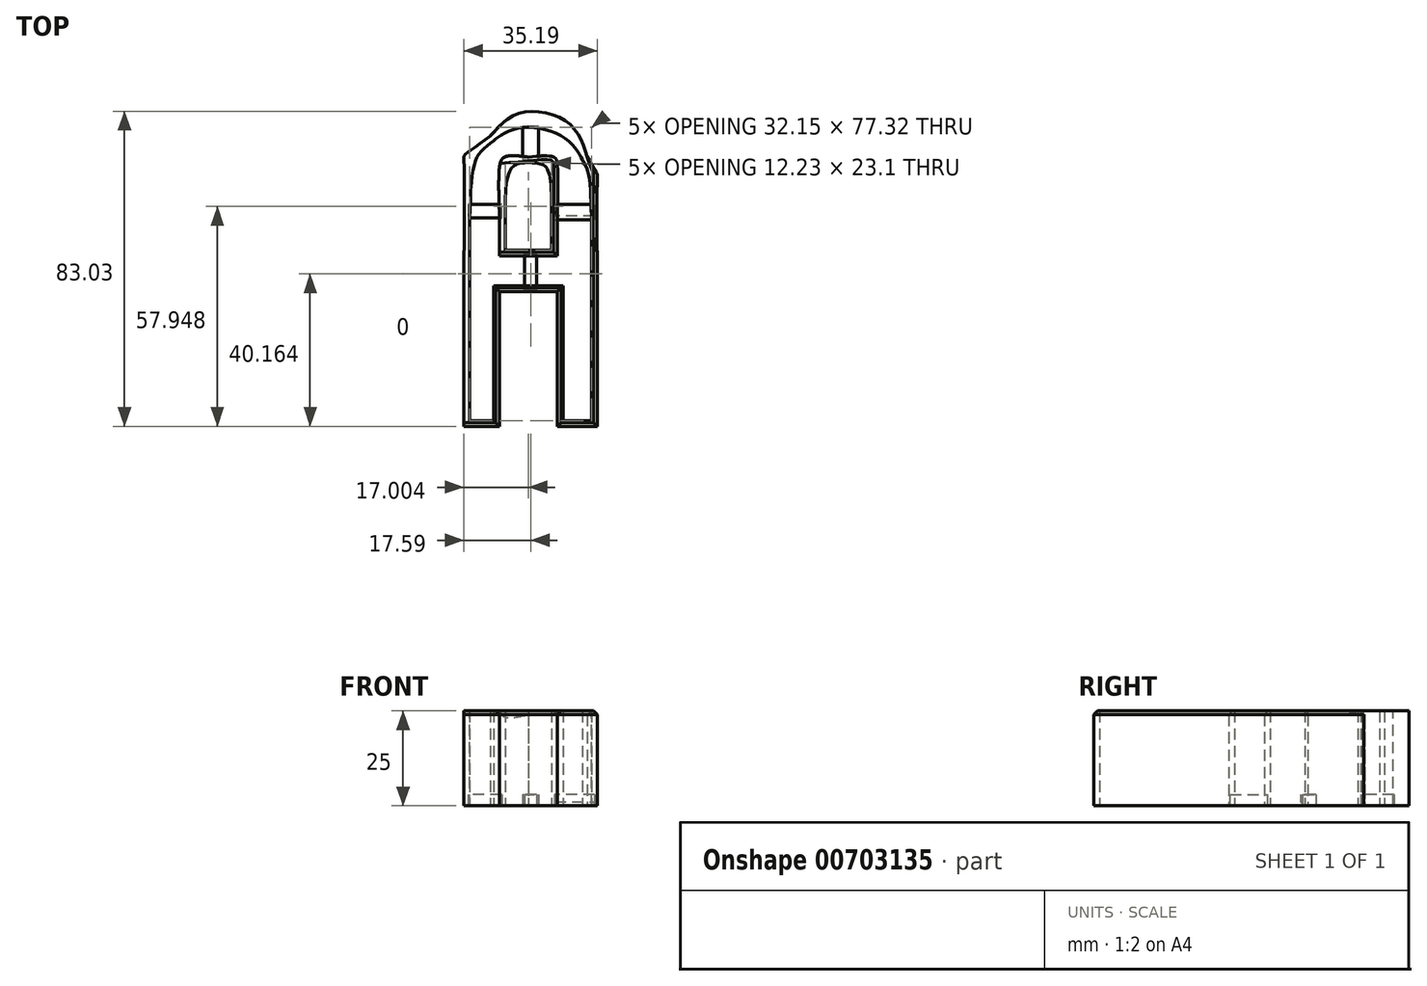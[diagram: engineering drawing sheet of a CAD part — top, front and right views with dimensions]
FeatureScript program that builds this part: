
annotation { "Feature Type Name" : "Feature", "Feature Type Description" : "" }
export const myFeature = defineFeature(function(context is Context, id is Id, definition is map)
    precondition{}
    {
        {
            var Q0;
            Q0=qCreatedBy(makeId("Top.planeOp"),FACE);
            var sketch = newSketch(context, id + "F0", { "sketchPlane" : qUnion([Q0])});
            skLineSegment(sketch, "E0", {"start": v(-8.2, -22.18) * mm, "end": v(-8.2, -4.43) * mm});
            skLineSegment(sketch, "E1", {"start": v(-8.2, -4.43) * mm, "end": v(-0.59, -4.43) * mm});
            skLineSegment(sketch, "E2", {"start": v(-0.59, -4.43) * mm, "end": v(7.03, -4.43) * mm});
            skLineSegment(sketch, "E3", {"start": v(7.03, -4.43) * mm, "end": v(7.03, -22.18) * mm});
            skLineSegment(sketch, "E4", {"start": v(7.03, -22.18) * mm, "end": v(7.03, -39.93) * mm});
            skLineSegment(sketch, "E5", {"start": v(7.03, -39.93) * mm, "end": v(12.3, -39.93) * mm});
            skLineSegment(sketch, "E6", {"start": v(12.3, -39.93) * mm, "end": v(17.58, -39.93) * mm});
            skLineSegment(sketch, "E7", {"start": v(17.58, -39.93) * mm, "end": v(17.58, -6.74) * mm});
            skFitSpline(sketch, "E8", {"points": [v(17.58, -6.74) * mm, v(17.58, 25.6) * mm, v(17.5, 26.57) * mm, v(14.94, 31.1) * mm]});
            skFitSpline(sketch, "E9", {"points": [v(14.94, 31.1) * mm, v(9.84, 40.13) * mm, v(-2.43, 42.74) * mm, v(-10.67, 36.56) * mm]});
            skFitSpline(sketch, "E10", {"points": [v(-10.67, 36.56) * mm, v(-17.53, 31.41) * mm, v(-17.58, 31.15) * mm, v(-17.58, -5.94) * mm]});
            skLineSegment(sketch, "E11", {"start": v(-17.58, -5.94) * mm, "end": v(-17.58, -39.93) * mm});
            skLineSegment(sketch, "E12", {"start": v(-17.58, -39.93) * mm, "end": v(-12.89, -39.93) * mm});
            skLineSegment(sketch, "E13", {"start": v(-12.89, -39.93) * mm, "end": v(-8.2, -39.93) * mm});
            skLineSegment(sketch, "E14", {"start": v(-8.2, -39.93) * mm, "end": v(-8.2, -22.18) * mm});
            skFitSpline(sketch, "E15", {"points": [v(-8.2, 15.7) * mm, v(-8.2, 28.37) * mm, v(-6.87, 31.07) * mm, v(-0.6, 31.07) * mm]});
            skFitSpline(sketch, "E16", {"points": [v(-0.6, 31.07) * mm, v(6.1, 31.07) * mm, v(7.03, 29.27) * mm, v(7.03, 16.38) * mm]});
            skLineSegment(sketch, "E17", {"start": v(7.03, 16.38) * mm, "end": v(7.03, 4.97) * mm});
            skLineSegment(sketch, "E18", {"start": v(7.03, 4.97) * mm, "end": v(-0.59, 4.97) * mm});
            skLineSegment(sketch, "E19", {"start": v(-0.59, 4.97) * mm, "end": v(-8.2, 4.97) * mm});
            skLineSegment(sketch, "E20", {"start": v(-8.2, 4.97) * mm, "end": v(-8.2, 15.7) * mm});
            skLineSegment(sketch, "E21.0", {"start": v(16.08, -38.43) * mm, "end": v(16.08, -6.74) * mm});
            skLineSegment(sketch, "E21.1", {"start": v(12.3, -38.43) * mm, "end": v(16.08, -38.43) * mm});
            skLineSegment(sketch, "E21.2", {"start": v(8.53, -38.43) * mm, "end": v(12.3, -38.43) * mm});
            skLineSegment(sketch, "E21.3", {"start": v(8.53, -22.18) * mm, "end": v(8.53, -38.43) * mm});
            skLineSegment(sketch, "E21.4", {"start": v(-16.08, -38.43) * mm, "end": v(-12.89, -38.43) * mm});
            skLineSegment(sketch, "E21.5", {"start": v(-16.08, -5.94) * mm, "end": v(-16.08, -38.43) * mm});
            skFitSpline(sketch, "E21.6", {"points": [v(-9.77, 35.36) * mm, v(-10.63, 34.71) * mm, v(-11.71, 33.9) * mm, v(-12.8, 32.87) * mm, v(-13.45, 32.1) * mm, v(-14, 31.22) * mm, v(-14.47, 30.16) * mm, v(-14.88, 28.81) * mm, v(-15.34, 26.55) * mm, v(-15.74, 22.7) * mm, v(-15.99, 16) * mm, v(-16.07, 6.81) * mm, v(-16.08, -1.3) * mm, v(-16.08, -5.94) * mm]});
            skFitSpline(sketch, "E21.7", {"points": [v(13.63, 30.37) * mm, v(12.47, 32.43) * mm, v(9.33, 35.8) * mm, v(3.09, 38.5) * mm, v(-3.7, 38.57) * mm, v(-7.9, 36.76) * mm, v(-9.77, 35.36) * mm]});
            skLineSegment(sketch, "E21.8", {"start": v(-12.89, -38.43) * mm, "end": v(-9.7, -38.43) * mm});
            skLineSegment(sketch, "E21.9", {"start": v(-9.7, -38.43) * mm, "end": v(-9.7, -22.18) * mm});
            skLineSegment(sketch, "E21.10", {"start": v(-9.7, -22.18) * mm, "end": v(-9.7, -2.93) * mm});
            skLineSegment(sketch, "E21.11", {"start": v(-9.7, -2.93) * mm, "end": v(-0.59, -2.93) * mm});
            skFitSpline(sketch, "E21.12", {"points": [v(16.08, -6.74) * mm, v(16.08, -2.7) * mm, v(16.07, 4.4) * mm, v(16.04, 12.52) * mm, v(15.93, 18.5) * mm, v(15.74, 22.73) * mm, v(15.44, 25.6) * mm, v(15.02, 27.48) * mm, v(14.47, 28.85) * mm, v(13.95, 29.81) * mm, v(13.63, 30.37) * mm]});
            skLineSegment(sketch, "E21.13", {"start": v(-0.59, -2.93) * mm, "end": v(8.53, -2.93) * mm});
            skLineSegment(sketch, "E21.14", {"start": v(8.53, -2.93) * mm, "end": v(8.53, -22.18) * mm});
            skLineSegment(sketch, "E22.0", {"start": v(-6.7, 6.47) * mm, "end": v(-6.7, 15.7) * mm});
            skFitSpline(sketch, "E22.1", {"points": [v(-0.6, 29.57) * mm, v(0.2, 29.57) * mm, v(1.25, 29.53) * mm, v(2.3, 29.36) * mm, v(2.93, 29.18) * mm, v(3.41, 28.96) * mm, v(3.78, 28.7) * mm, v(4.1, 28.37) * mm, v(4.4, 27.9) * mm, v(4.68, 27.25) * mm, v(5.01, 26.1) * mm, v(5.32, 24.12) * mm, v(5.5, 20.83) * mm, v(5.53, 17.98) * mm, v(5.53, 16.38) * mm]});
            skLineSegment(sketch, "E22.2", {"start": v(5.53, 16.38) * mm, "end": v(5.53, 6.47) * mm});
            skFitSpline(sketch, "E22.3", {"points": [v(-6.7, 15.7) * mm, v(-6.7, 17.27) * mm, v(-6.66, 20.09) * mm, v(-6.44, 23.42) * mm, v(-6.02, 25.91) * mm, v(-5.53, 27.3) * mm, v(-5.07, 28.07) * mm, v(-4.71, 28.5) * mm, v(-4.31, 28.82) * mm, v(-3.84, 29.09) * mm, v(-3.25, 29.3) * mm, v(-2.28, 29.5) * mm, v(-1.33, 29.57) * mm, v(-0.6, 29.57) * mm]});
            skLineSegment(sketch, "E22.4", {"start": v(5.53, 6.47) * mm, "end": v(-0.59, 6.47) * mm});
            skLineSegment(sketch, "E22.5", {"start": v(-0.59, 6.47) * mm, "end": v(-6.7, 6.47) * mm});
            skSolve(sketch);
        }
        {
            var Q0;
            Q0=makeQuery(id+"F0.imprint","IMPRINT",FACE,{"disambiguationData":[TD([[makeQuery(id+"F0.imprint","IMPRINT",EDGE,{"derivedFrom":sQuery(id+"F0.wireOp",EDGE,"E0")}),1.0]])]});
            var Q1;
            Q1=makeQuery(id+"F0.imprint","IMPRINT",FACE,{"disambiguationData":[TD([[makeQuery(id+"F0.imprint","IMPRINT",EDGE,{"derivedFrom":sQuery(id+"F0.wireOp",EDGE,"E15")}),-1.0]])]});
            extrude(context, id + "F1", {"entities" : qUnion([Q0, Q1]), "depth" : 25 * mm, "offsetDistance" : 25 * mm});
        }
        {
            var Q0;
            Q0=qCreatedBy(makeId("Top.planeOp"),FACE);
            var sketch = newSketch(context, id + "F2", { "sketchPlane" : qUnion([Q0])});
            skLineSegment(sketch, "E23", {"start": v(1.61, -4.13) * mm, "end": v(1.61, 5.73) * mm});
            skLineSegment(sketch, "E24", {"start": v(1.61, -4.13) * mm, "end": v(-1.61, -4.13) * mm});
            skLineSegment(sketch, "E25", {"start": v(-1.61, -4.13) * mm, "end": v(-1.61, 5.73) * mm});
            skLineSegment(sketch, "E26", {"start": v(-1.61, 5.73) * mm, "end": v(1.61, 5.73) * mm});
            skLineSegment(sketch, "E27", {"start": v(-2.12, 30.36) * mm, "end": v(2.12, 30.36) * mm});
            skLineSegment(sketch, "E28", {"start": v(2.12, 30.36) * mm, "end": v(2.12, 39.11) * mm});
            skLineSegment(sketch, "E29", {"start": v(2.12, 39.11) * mm, "end": v(-2.12, 39.11) * mm});
            skLineSegment(sketch, "E30", {"start": v(-2.12, 39.11) * mm, "end": v(-2.12, 30.36) * mm});
            skLineSegment(sketch, "E31", {"start": v(-7.62, 18.59) * mm, "end": v(-16.42, 18.59) * mm});
            skLineSegment(sketch, "E32", {"start": v(-16.42, 18.59) * mm, "end": v(-16.42, 15.05) * mm});
            skLineSegment(sketch, "E33", {"start": v(-16.42, 15.05) * mm, "end": v(-7.62, 15.05) * mm});
            skLineSegment(sketch, "E34", {"start": v(-7.62, 15.05) * mm, "end": v(-7.62, 18.59) * mm});
            skLineSegment(sketch, "E35", {"start": v(6.32, 18.59) * mm, "end": v(6.32, 14.5) * mm});
            skLineSegment(sketch, "E36", {"start": v(6.32, 14.5) * mm, "end": v(16.88, 14.5) * mm});
            skLineSegment(sketch, "E37", {"start": v(16.88, 14.5) * mm, "end": v(16.88, 18.59) * mm});
            skLineSegment(sketch, "E38", {"start": v(16.88, 18.59) * mm, "end": v(6.32, 18.59) * mm});
            skSolve(sketch);
        }
        {
            var Q0;
            Q0=makeQuery(id+"F2.imprint","IMPRINT",FACE,{"disambiguationData":[TD([[makeQuery(id+"F2.imprint","IMPRINT",EDGE,{"derivedFrom":sQuery(id+"F2.wireOp",EDGE,"E23")}),1.0]])]});
            var Q1;
            Q1=makeQuery(id+"F2.imprint","IMPRINT",FACE,{"disambiguationData":[TD([[makeQuery(id+"F2.imprint","IMPRINT",EDGE,{"derivedFrom":sQuery(id+"F2.wireOp",EDGE,"E27")}),1.0]])]});
            var Q2;
            Q2=makeQuery(id+"F2.imprint","IMPRINT",FACE,{"disambiguationData":[TD([[makeQuery(id+"F2.imprint","IMPRINT",EDGE,{"derivedFrom":sQuery(id+"F2.wireOp",EDGE,"E31")}),1.0]])]});
            var Q3;
            Q3=makeQuery(id+"F2.imprint","IMPRINT",FACE,{"disambiguationData":[TD([[makeQuery(id+"F2.imprint","IMPRINT",EDGE,{"derivedFrom":sQuery(id+"F2.wireOp",EDGE,"E35")}),1.0]])]});
            extrude(context, id + "F3", {"entities" : qUnion([Q0, Q1, Q2, Q3]), "depth" : 3 * mm, "offsetDistance" : 25 * mm});
        }
        {
            var Q0;
            Q0=makeQuery(id+"F1.opExtrude","CAP_EDGE",EDGE,{"disambiguationData":[OSD([sQuery(id+"F0.wireOp",EDGE,"E8")])],"isStart":false});
            var Q1;
            Q1=makeQuery(id+"F1.opExtrude","CAP_EDGE",EDGE,{"disambiguationData":[OSD([sQuery(id+"F0.wireOp",EDGE,"E12"),sQuery(id+"F0.wireOp",EDGE,"E13")])],"isStart":false});
            var Q2;
            Q2=makeQuery(id+"F1.opExtrude","CAP_EDGE",EDGE,{"disambiguationData":[OSD([sQuery(id+"F0.wireOp",EDGE,"E0"),sQuery(id+"F0.wireOp",EDGE,"E14")])],"isStart":false});
            var Q3;
            Q3=makeQuery(id+"F1.opExtrude","CAP_EDGE",EDGE,{"disambiguationData":[OSD([sQuery(id+"F0.wireOp",EDGE,"E1"),sQuery(id+"F0.wireOp",EDGE,"E2")])],"isStart":false});
            var Q4;
            Q4=makeQuery(id+"F1.opExtrude","CAP_EDGE",EDGE,{"disambiguationData":[OSD([sQuery(id+"F0.wireOp",EDGE,"E3"),sQuery(id+"F0.wireOp",EDGE,"E4")])],"isStart":false});
            var Q5;
            Q5=makeQuery(id+"F1.opExtrude","CAP_EDGE",EDGE,{"disambiguationData":[OSD([sQuery(id+"F0.wireOp",EDGE,"E5"),sQuery(id+"F0.wireOp",EDGE,"E6")])],"isStart":false});
            var Q6;
            Q6=makeQuery(id+"F1.opExtrude","CAP_EDGE",EDGE,{"disambiguationData":[OSD([sQuery(id+"F0.wireOp",EDGE,"E18"),sQuery(id+"F0.wireOp",EDGE,"E19")])],"isStart":false});
            var Q7;
            Q7=makeQuery(id+"F3.opExtrude","CAP_EDGE",EDGE,{"disambiguationData":[OSD([sQuery(id+"F2.wireOp",EDGE,"E36")])],"isStart":true});
            var Q8;
            Q8=makeQuery(id+"F1.opExtrude","CAP_EDGE",EDGE,{"disambiguationData":[OSD([sQuery(id+"F0.wireOp",EDGE,"E16")])],"isStart":false});
            chamfer(context, id + "F4", {"entities" : qUnion([Q0, Q1, Q2, Q3, Q4, Q5, Q6, Q7, Q8]), "width" : 1 * mm, "tangentPropagation" : true});
        }
    });
